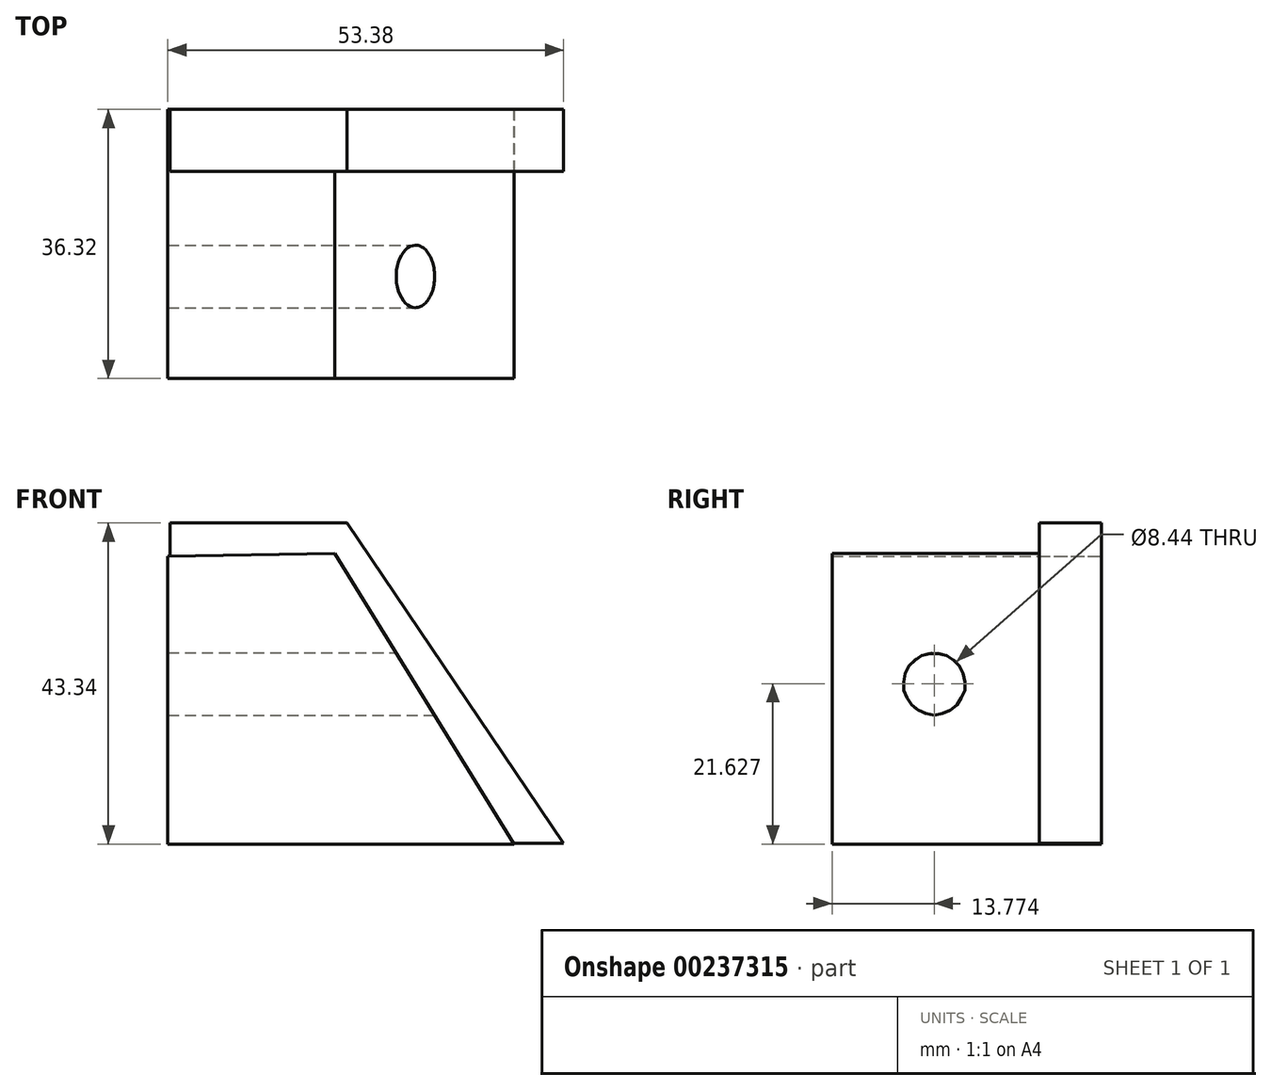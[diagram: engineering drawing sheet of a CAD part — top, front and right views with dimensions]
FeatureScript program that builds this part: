
annotation { "Feature Type Name" : "Feature", "Feature Type Description" : "" }
export const myFeature = defineFeature(function(context is Context, id is Id, definition is map)
    precondition{}
    {
        {
            var Q0;
            Q0=qCreatedBy(makeId("Front.planeOp"),FACE);
            var sketch = newSketch(context, id + "F0", { "sketchPlane" : qUnion([Q0])});
            skLineSegment(sketch, "E0", {"start": v(-37.4, 24.29) * mm, "end": v(-37.4, -14.57) * mm});
            skLineSegment(sketch, "E1", {"start": v(-37.4, -14.57) * mm, "end": v(9.35, -14.57) * mm});
            skLineSegment(sketch, "E2", {"start": v(9.35, -14.57) * mm, "end": v(-14.85, 24.65) * mm});
            skLineSegment(sketch, "E3", {"start": v(-14.85, 24.65) * mm, "end": v(-37.4, 24.29) * mm});
            skSolve(sketch);
        }
        {
            var Q0;
            Q0=makeQuery(id+"F0.imprint","IMPRINT",FACE,{"disambiguationData":[TD([[makeQuery(id+"F0.imprint","IMPRINT",EDGE,{"derivedFrom":sQuery(id+"F0.wireOp",EDGE,"E0")}),1.0]])]});
            extrude(context, id + "F1", {"entities" : qUnion([Q0]), "depth" : 36.32 * mm});
        }
        {
            var Q0;
            Q0=qCreatedBy(makeId("Front.planeOp"),FACE);
            var sketch = newSketch(context, id + "F2", { "sketchPlane" : qUnion([Q0])});
            skLineSegment(sketch, "E4", {"start": v(-37.07, 24.74) * mm, "end": v(-37.07, 28.77) * mm});
            skLineSegment(sketch, "E5", {"start": v(-37.07, 28.77) * mm, "end": v(-13.21, 28.77) * mm});
            skLineSegment(sketch, "E6", {"start": v(-13.21, 28.77) * mm, "end": v(15.99, -14.49) * mm});
            skLineSegment(sketch, "E7", {"start": v(15.99, -14.49) * mm, "end": v(9.13, -14.49) * mm});
            skLineSegment(sketch, "E8", {"start": v(9.13, -14.49) * mm, "end": v(-36.9, -14.49) * mm});
            skLineSegment(sketch, "E9", {"start": v(-36.9, -14.49) * mm, "end": v(-37.07, 24.74) * mm});
            skSolve(sketch);
        }
        {
            var Q0;
            Q0=makeQuery(id+"F2.imprint","IMPRINT",FACE,{"disambiguationData":[TD([[makeQuery(id+"F2.imprint","IMPRINT",EDGE,{"derivedFrom":sQuery(id+"F2.wireOp",EDGE,"E4")}),-1.0]])]});
            extrude(context, id + "F3", {"entities" : qUnion([Q0]), "operationType" : NewBodyOperationType.ADD, "depth" : 8.38 * mm});
        }
        {
            var Q0;
            Q0=qCreatedBy(makeId("Right.planeOp"),FACE);
            var sketch = newSketch(context, id + "F4", { "sketchPlane" : qUnion([Q0])});
            skCircle(sketch, "E10", {"center": v(-22.55, 7.06) * mm, "radius": 4.22 * mm});
            skSolve(sketch);
        }
        {
            var Q0;
            Q0=makeQuery(id+"F4.imprint","IMPRINT",FACE,{"disambiguationData":[TD([[makeQuery(id+"F4.imprint","IMPRINT",EDGE,{"derivedFrom":sQuery(id+"F4.wireOp",EDGE,"E10")}),1.0]])]});
            extrude(context, id + "F5", {"entities" : qUnion([Q0]), "operationType" : NewBodyOperationType.REMOVE, "oppositeDirection" : true, "depth" : 46.74 * mm});
        }
    });
